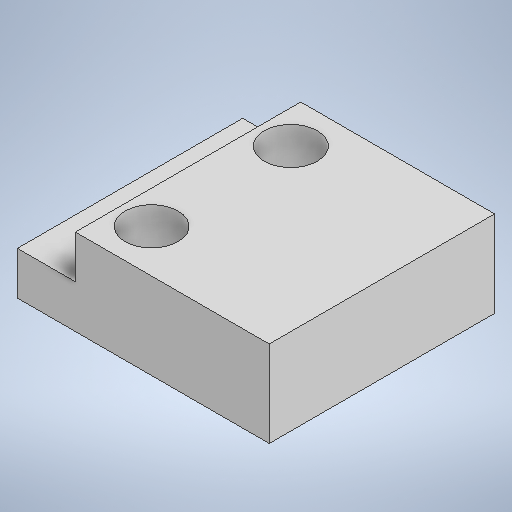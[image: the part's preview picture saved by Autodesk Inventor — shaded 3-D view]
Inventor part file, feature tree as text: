
AUTODESK INVENTOR PART (.ipt)
format: ipt  version: 2025.1 (Build 291241000, 241)  size: 228,352 bytes
history: native  units: in
note: dims shown in document units (in); Inventor stores cm internally (conversion verified against a paired STEP export)
features: extrude x2, sketch x2
ambient origin geometry x8: Origin, YZ Plane, XZ Plane, XY Plane, X Axis, Y Axis, Z Axis, Center Point
bodies: Solid1 (feature_tree)
feature tree (4):
  extrude  "Extrusion1"  Depth=0.5984in
  extrude  "Extrusion3"  Depth=0.1024in
  sketch  "Sketch1"  dims[d0=0.5354in d1=0.5984in]
  sketch  "Sketch2"  dims[d2=0.126in d3=0.1024in d4=0.1024in d5=0.2165in d7=0.1024in d8=0.0in d9=0.1378in d12=0.1024in d13=0.0in]
